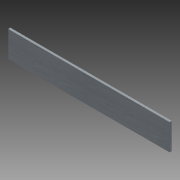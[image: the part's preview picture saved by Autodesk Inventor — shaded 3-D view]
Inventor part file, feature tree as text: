
AUTODESK INVENTOR PART (.ipt)
format: ipt  version: 2011 SP1 (Build 150282100, 282)  size: 75,264 bytes
history: native  units: in
note: dims shown in document units (in); Inventor stores cm internally (conversion verified against a paired STEP export)
features: extrude x1, sketch x1
ambient origin geometry x8: Origin, YZ Plane, XZ Plane, XY Plane, X Axis, Y Axis, Z Axis, Center Point
bodies: Solid1 (feature_tree)
feature tree (2):
  extrude  "Extrusion1"  Depth=4.625in
  sketch  "Sketch1"  dims[d0=9.25in d1=4.625in d2=1.5in d3=0.75in d4=0.125in d5=0.0in]
